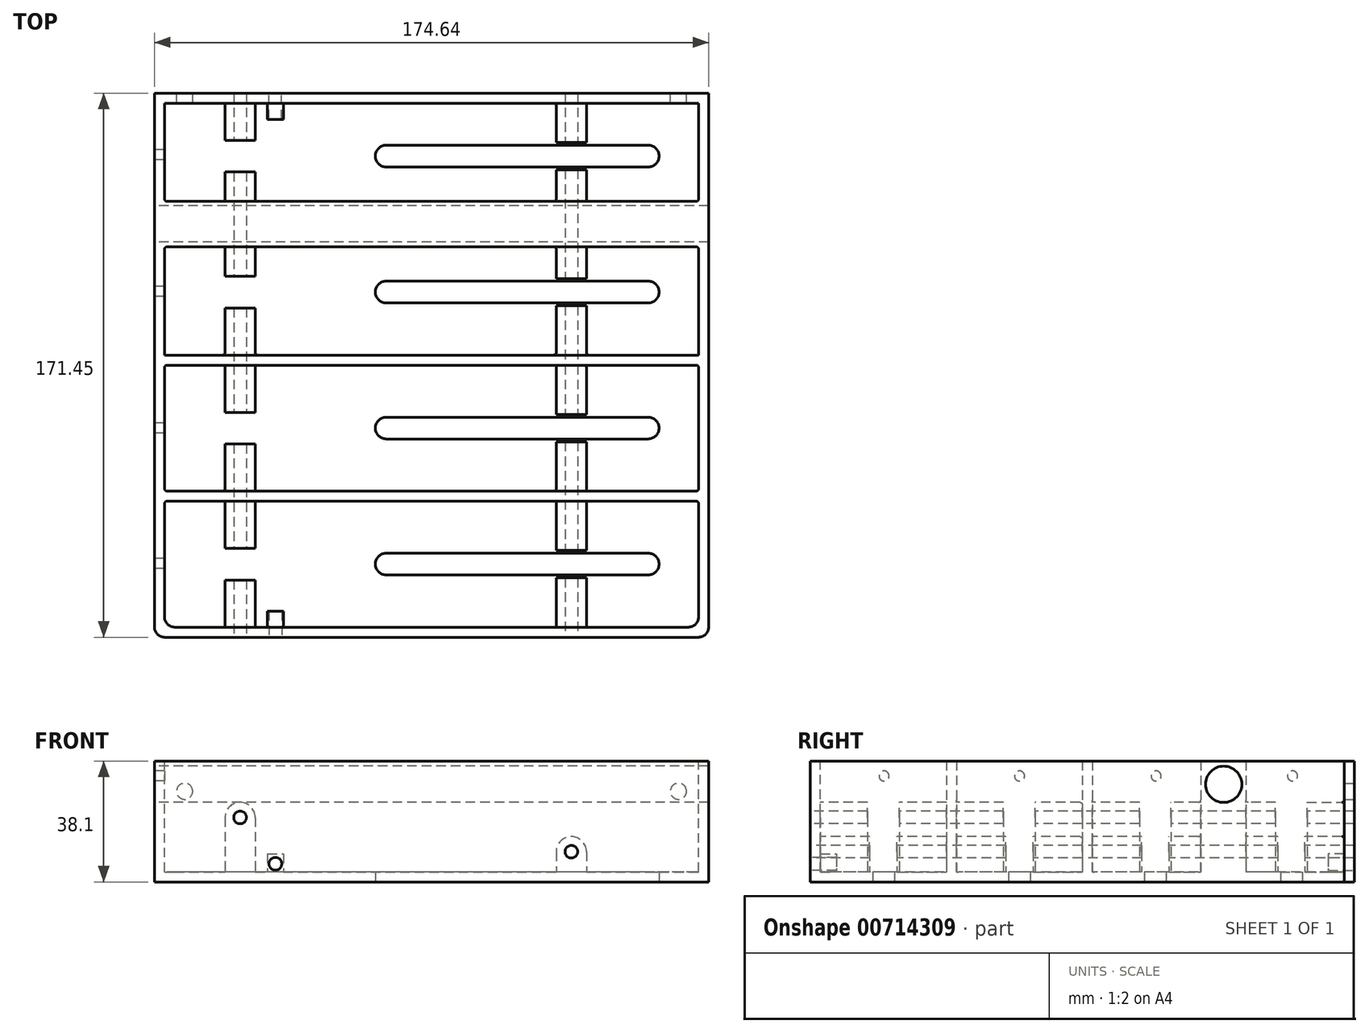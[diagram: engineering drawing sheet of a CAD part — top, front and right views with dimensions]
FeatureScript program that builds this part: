
annotation { "Feature Type Name" : "Feature", "Feature Type Description" : "" }
export const myFeature = defineFeature(function(context is Context, id is Id, definition is map)
    precondition{}
    {
        {
            var Q0;
            Q0=qCreatedBy(makeId("Top.planeOp"),FACE);
            var sketch = newSketch(context, id + "F0", { "sketchPlane" : qUnion([Q0])});
            skLineSegment(sketch, "E0.bottom", {"start": v(0, 0) * mm, "end": v(174.63, 0) * mm});
            skLineSegment(sketch, "E0.top", {"start": v(0, 174.63) * mm, "end": v(174.62, 174.63) * mm});
            skLineSegment(sketch, "E0.left", {"start": v(0, 0) * mm, "end": v(0, 174.63) * mm});
            skLineSegment(sketch, "E0.right", {"start": v(174.63, 0) * mm, "end": v(174.62, 174.63) * mm});
            skSolve(sketch);
        }
        {
            var Q0;
            Q0 = qSketchRegion(id + "F0", true);
            extrude(context, id + "F1", {"entities" : qUnion([Q0]), "depth" : 38.1 * mm, "offsetDistance" : 25.4 * mm});
        }
        {
            var Q0;
            Q0=makeQuery(id+"F1.opExtrude","CAP_FACE",FACE,{"disambiguationData":[OSD([sQuery(id+"F0.wireOp",EDGE,"E0.bottom"),sQuery(id+"F0.wireOp",EDGE,"E0.top"),sQuery(id+"F0.wireOp",EDGE,"E0.left"),sQuery(id+"F0.wireOp",EDGE,"E0.right")])],"isStart":false});
            var sketch = newSketch(context, id + "F2", { "sketchPlane" : qUnion([Q0])});
            skLineSegment(sketch, "E1.bottom", {"start": v(3.17, 171.45) * mm, "end": v(171.45, 171.45) * mm});
            skLineSegment(sketch, "E1.top", {"start": v(3.18, 3.18) * mm, "end": v(171.45, 3.18) * mm});
            skLineSegment(sketch, "E1.left", {"start": v(3.17, 171.45) * mm, "end": v(3.18, 3.17) * mm});
            skLineSegment(sketch, "E1.right", {"start": v(171.45, 171.45) * mm, "end": v(171.45, 3.18) * mm});
            skSolve(sketch);
        }
        {
            var Q0;
            Q0 = qSketchRegion(id + "F2", true);
            extrude(context, id + "F3", {"entities" : qUnion([Q0]), "operationType" : NewBodyOperationType.REMOVE, "oppositeDirection" : true, "depth" : 34.92 * mm, "offsetDistance" : 25.4 * mm});
        }
        {
            var Q0;
            Q0=makeQuery(id+"F3.boolean.opBoolean","COPY",EDGE,{"derivedFrom":makeQuery(id+"F3.opExtrude","SWEPT_EDGE",EDGE,{"disambiguationData":[OSD([sQuery(id+"F2.wireOp",EDGE,"E1.bottom"),sQuery(id+"F2.wireOp",EDGE,"E1.right")])]})});
            var Q1;
            Q1=makeQuery(id+"F3.boolean.opBoolean","COPY",EDGE,{"derivedFrom":makeQuery(id+"F3.opExtrude","SWEPT_EDGE",EDGE,{"disambiguationData":[OSD([sQuery(id+"F2.wireOp",EDGE,"E1.top"),sQuery(id+"F2.wireOp",EDGE,"E1.right")])]})});
            var Q2;
            Q2=makeQuery(id+"F3.boolean.opBoolean","COPY",EDGE,{"derivedFrom":makeQuery(id+"F3.opExtrude","SWEPT_EDGE",EDGE,{"disambiguationData":[OSD([sQuery(id+"F2.wireOp",EDGE,"E1.bottom"),sQuery(id+"F2.wireOp",EDGE,"E1.left")])]})});
            var Q3;
            Q3=makeQuery(id+"F3.boolean.opBoolean","COPY",EDGE,{"derivedFrom":makeQuery(id+"F3.opExtrude","SWEPT_EDGE",EDGE,{"disambiguationData":[OSD([sQuery(id+"F2.wireOp",EDGE,"E1.top"),sQuery(id+"F2.wireOp",EDGE,"E1.left")])]})});
            var Q4;
            Q4=makeQuery(id+"F1.opExtrude","SWEPT_EDGE",EDGE,{"disambiguationData":[OSD([sQuery(id+"F0.wireOp",EDGE,"E0.top"),sQuery(id+"F0.wireOp",EDGE,"E0.right")])]});
            var Q5;
            Q5=makeQuery(id+"F1.opExtrude","SWEPT_EDGE",EDGE,{"disambiguationData":[OSD([sQuery(id+"F0.wireOp",EDGE,"E0.top"),sQuery(id+"F0.wireOp",EDGE,"E0.left")])]});
            var Q6;
            Q6=makeQuery(id+"F1.opExtrude","SWEPT_EDGE",EDGE,{"disambiguationData":[OSD([sQuery(id+"F0.wireOp",EDGE,"E0.bottom"),sQuery(id+"F0.wireOp",EDGE,"E0.right")])]});
            var Q7;
            Q7=makeQuery(id+"F1.opExtrude","SWEPT_EDGE",EDGE,{"disambiguationData":[OSD([sQuery(id+"F0.wireOp",EDGE,"E0.bottom"),sQuery(id+"F0.wireOp",EDGE,"E0.left")])]});
            fillet(context, id + "F4", {"entities" : qUnion([Q0, Q1, Q2, Q3, Q4, Q5, Q6, Q7]), "radius" : 3.17 * mm, "tangentPropagation" : true, "allowEdgeOverflow" : false});
        }
        {
            var Q0;
            Q0=qCreatedBy(makeId("Top.planeOp"),FACE);
            var sketch = newSketch(context, id + "F5", { "sketchPlane" : qUnion([Q0])});
            skLineSegment(sketch, "E2.bottom", {"start": v(3.36, 131.76) * mm, "end": v(171.33, 131.76) * mm});
            skLineSegment(sketch, "E2.top", {"start": v(3.36, 128.59) * mm, "end": v(171.33, 128.59) * mm});
            skLineSegment(sketch, "E2.left", {"start": v(3.36, 131.76) * mm, "end": v(3.36, 128.59) * mm});
            skLineSegment(sketch, "E2.right", {"start": v(171.33, 131.76) * mm, "end": v(171.33, 128.59) * mm});
            skLineSegment(sketch, "E3.bottom", {"start": v(3.17, 88.9) * mm, "end": v(171.45, 88.9) * mm});
            skLineSegment(sketch, "E3.top", {"start": v(3.17, 85.72) * mm, "end": v(171.45, 85.72) * mm});
            skLineSegment(sketch, "E3.left", {"start": v(3.17, 88.9) * mm, "end": v(3.17, 85.72) * mm});
            skLineSegment(sketch, "E3.right", {"start": v(171.45, 88.9) * mm, "end": v(171.45, 85.73) * mm});
            skLineSegment(sketch, "E4.bottom", {"start": v(3.18, 46.04) * mm, "end": v(171.45, 46.04) * mm});
            skLineSegment(sketch, "E4.top", {"start": v(3.18, 42.86) * mm, "end": v(171.45, 42.86) * mm});
            skLineSegment(sketch, "E4.left", {"start": v(3.18, 46.04) * mm, "end": v(3.18, 42.86) * mm});
            skLineSegment(sketch, "E4.right", {"start": v(171.45, 46.04) * mm, "end": v(171.45, 42.86) * mm});
            skSolve(sketch);
        }
        {
            var Q0;
            Q0 = qSketchRegion(id + "F5", true);
            extrude(context, id + "F6", {"entities" : qUnion([Q0]), "operationType" : NewBodyOperationType.ADD, "depth" : 38.1 * mm, "offsetDistance" : 25.4 * mm});
        }
        {
            var Q0;
            Q0=qCreatedBy(makeId("Top.planeOp"),FACE);
            var sketch = newSketch(context, id + "F7", { "sketchPlane" : qUnion([Q0])});
            skLineSegment(sketch, "E5", {"start": v(73.02, 155.03) * mm, "end": v(155.57, 155.03) * mm});
            skArc(sketch, "E6", {"start": v(155.57, 148.17) * mm, "mid": v(159, 151.6) * mm, "end": v(155.57, 155.03) * mm});
            skLineSegment(sketch, "E7", {"start": v(155.57, 148.17) * mm, "end": v(73.02, 148.17) * mm});
            skArc(sketch, "E8", {"start": v(73.02, 155.03) * mm, "mid": v(69.6, 151.6) * mm, "end": v(73.02, 148.17) * mm});
            skLineSegment(sketch, "E9.0.1.0", {"start": v(155.57, 105.32) * mm, "end": v(73.02, 105.32) * mm});
            skArc(sketch, "E9.0.1.1", {"start": v(155.57, 105.32) * mm, "mid": v(159, 108.75) * mm, "end": v(155.57, 112.18) * mm});
            skLineSegment(sketch, "E9.0.1.2", {"start": v(73.02, 112.18) * mm, "end": v(155.57, 112.18) * mm});
            skArc(sketch, "E9.0.1.3", {"start": v(73.02, 112.18) * mm, "mid": v(69.6, 108.75) * mm, "end": v(73.02, 105.32) * mm});
            skLineSegment(sketch, "E9.0.2.0", {"start": v(155.57, 62.47) * mm, "end": v(73.02, 62.47) * mm});
            skArc(sketch, "E9.0.2.1", {"start": v(155.57, 62.47) * mm, "mid": v(159, 65.9) * mm, "end": v(155.57, 69.33) * mm});
            skLineSegment(sketch, "E9.0.2.2", {"start": v(73.02, 69.33) * mm, "end": v(155.57, 69.33) * mm});
            skArc(sketch, "E9.0.2.3", {"start": v(73.02, 69.33) * mm, "mid": v(69.6, 65.9) * mm, "end": v(73.02, 62.47) * mm});
            skLineSegment(sketch, "E9.0.3.0", {"start": v(155.57, 19.62) * mm, "end": v(73.02, 19.62) * mm});
            skArc(sketch, "E9.0.3.1", {"start": v(155.57, 19.62) * mm, "mid": v(159, 23.05) * mm, "end": v(155.57, 26.48) * mm});
            skLineSegment(sketch, "E9.0.3.2", {"start": v(73.02, 26.48) * mm, "end": v(155.57, 26.48) * mm});
            skArc(sketch, "E9.0.3.3", {"start": v(73.02, 26.48) * mm, "mid": v(69.6, 23.05) * mm, "end": v(73.02, 19.62) * mm});
            skLineSegment(sketch, "E9.direction1", {"start": v(73.02, 148.17) * mm, "end": v(73.02, 148.17) * mm});
            skLineSegment(sketch, "E9.direction2", {"start": v(73.02, 148.17) * mm, "end": v(73.02, 105.32) * mm, "construction": true});
            skSolve(sketch);
        }
        {
            var Q0;
            Q0 = qSketchRegion(id + "F7", true);
            extrude(context, id + "F8", {"entities" : qUnion([Q0]), "operationType" : NewBodyOperationType.REMOVE, "depth" : 5.08 * mm, "offsetDistance" : 25.4 * mm});
        }
        {
            var Q0;
            Q0=makeQuery(id+"F1.opExtrude","SWEPT_FACE",FACE,{"disambiguationData":[OSD([sQuery(id+"F0.wireOp",EDGE,"E0.bottom")])]});
            var sketch = newSketch(context, id + "F9", { "sketchPlane" : qUnion([Q0])});
            skCircle(sketch, "E10", {"center": v(131.36, 9.53) * mm, "radius": 2 * mm});
            skCircle(sketch, "E11", {"center": v(26.99, 20.32) * mm, "radius": 2 * mm});
            skSolve(sketch);
        }
        {
            var Q0;
            Q0=qCreatedBy(makeId("Top.planeOp"),FACE);
            var sketch = newSketch(context, id + "F10", { "sketchPlane" : qUnion([Q0])});
            skLineSegment(sketch, "E12.bottom", {"start": v(22.23, 3.18) * mm, "end": v(31.75, 3.18) * mm});
            skLineSegment(sketch, "E12.top", {"start": v(22.23, 18.03) * mm, "end": v(31.75, 18.03) * mm});
            skLineSegment(sketch, "E12.left", {"start": v(22.23, 3.18) * mm, "end": v(22.23, 18.03) * mm});
            skLineSegment(sketch, "E12.right", {"start": v(31.75, 3.18) * mm, "end": v(31.75, 18.03) * mm});
            skLineSegment(sketch, "E13.bottom", {"start": v(22.23, 42.86) * mm, "end": v(31.75, 42.86) * mm});
            skLineSegment(sketch, "E13.top", {"start": v(22.23, 28) * mm, "end": v(31.75, 28) * mm});
            skLineSegment(sketch, "E13.left", {"start": v(22.23, 42.86) * mm, "end": v(22.23, 28) * mm});
            skLineSegment(sketch, "E13.right", {"start": v(31.75, 42.86) * mm, "end": v(31.75, 28) * mm});
            skLineSegment(sketch, "E14.0.1.0", {"start": v(31.75, 46.02) * mm, "end": v(31.75, 60.88) * mm});
            skLineSegment(sketch, "E14.0.1.1", {"start": v(22.23, 60.88) * mm, "end": v(31.75, 60.88) * mm});
            skLineSegment(sketch, "E14.0.1.2", {"start": v(22.23, 46.02) * mm, "end": v(22.23, 60.88) * mm});
            skLineSegment(sketch, "E14.0.1.3", {"start": v(22.23, 46.02) * mm, "end": v(31.75, 46.02) * mm});
            skLineSegment(sketch, "E14.0.1.4", {"start": v(22.23, 70.85) * mm, "end": v(31.75, 70.85) * mm});
            skLineSegment(sketch, "E14.0.1.5", {"start": v(31.75, 85.71) * mm, "end": v(31.75, 70.85) * mm});
            skLineSegment(sketch, "E14.0.1.6", {"start": v(22.23, 85.71) * mm, "end": v(22.23, 70.85) * mm});
            skLineSegment(sketch, "E14.0.1.7", {"start": v(22.23, 85.71) * mm, "end": v(31.75, 85.71) * mm});
            skLineSegment(sketch, "E14.0.2.0", {"start": v(31.75, 88.87) * mm, "end": v(31.75, 103.73) * mm});
            skLineSegment(sketch, "E14.0.2.1", {"start": v(22.23, 103.73) * mm, "end": v(31.75, 103.73) * mm});
            skLineSegment(sketch, "E14.0.2.2", {"start": v(22.23, 88.87) * mm, "end": v(22.23, 103.73) * mm});
            skLineSegment(sketch, "E14.0.2.3", {"start": v(22.23, 88.87) * mm, "end": v(31.75, 88.87) * mm});
            skLineSegment(sketch, "E14.0.2.4", {"start": v(22.23, 113.7) * mm, "end": v(31.75, 113.7) * mm});
            skLineSegment(sketch, "E14.0.2.5", {"start": v(31.75, 128.56) * mm, "end": v(31.75, 113.7) * mm});
            skLineSegment(sketch, "E14.0.2.6", {"start": v(22.23, 128.56) * mm, "end": v(22.23, 113.7) * mm});
            skLineSegment(sketch, "E14.0.2.7", {"start": v(22.23, 128.56) * mm, "end": v(31.75, 128.56) * mm});
            skLineSegment(sketch, "E14.0.3.0", {"start": v(31.75, 131.72) * mm, "end": v(31.75, 146.58) * mm});
            skLineSegment(sketch, "E14.0.3.1", {"start": v(22.23, 146.58) * mm, "end": v(31.75, 146.58) * mm});
            skLineSegment(sketch, "E14.0.3.2", {"start": v(22.23, 131.72) * mm, "end": v(22.23, 146.58) * mm});
            skLineSegment(sketch, "E14.0.3.3", {"start": v(22.23, 131.72) * mm, "end": v(31.75, 131.72) * mm});
            skLineSegment(sketch, "E14.0.3.4", {"start": v(22.23, 156.55) * mm, "end": v(31.75, 156.55) * mm});
            skLineSegment(sketch, "E14.0.3.5", {"start": v(31.75, 171.41) * mm, "end": v(31.75, 156.55) * mm});
            skLineSegment(sketch, "E14.0.3.6", {"start": v(22.23, 171.41) * mm, "end": v(22.23, 156.55) * mm});
            skLineSegment(sketch, "E14.0.3.7", {"start": v(22.23, 171.41) * mm, "end": v(31.75, 171.41) * mm});
            skLineSegment(sketch, "E14.direction1", {"start": v(31.75, 3.18) * mm, "end": v(31.75, 3.18) * mm});
            skSolve(sketch);
        }
        {
            var Q0;
            Q0 = qSketchRegion(id + "F10", true);
            extrude(context, id + "F11", {"entities" : qUnion([Q0]), "operationType" : NewBodyOperationType.ADD, "depth" : 25.1 * mm, "offsetDistance" : 25.4 * mm});
        }
        {
            var Q0;
            Q0=makeQuery(id+"F11.opExtrude","CAP_EDGE",EDGE,{"disambiguationData":[OSD([sQuery(id+"F10.wireOp",EDGE,"E14.0.3.6")])],"isStart":false});
            var Q1;
            Q1=makeQuery(id+"F11.opExtrude","CAP_EDGE",EDGE,{"disambiguationData":[OSD([sQuery(id+"F10.wireOp",EDGE,"E14.0.3.5")])],"isStart":false});
            var Q2;
            Q2=makeQuery(id+"F11.opExtrude","CAP_EDGE",EDGE,{"disambiguationData":[OSD([sQuery(id+"F10.wireOp",EDGE,"E14.0.3.0")])],"isStart":false});
            var Q3;
            Q3=makeQuery(id+"F11.opExtrude","CAP_EDGE",EDGE,{"disambiguationData":[OSD([sQuery(id+"F10.wireOp",EDGE,"E14.0.3.2")])],"isStart":false});
            var Q4;
            Q4=makeQuery(id+"F11.opExtrude","CAP_EDGE",EDGE,{"disambiguationData":[OSD([sQuery(id+"F10.wireOp",EDGE,"E14.0.2.5")])],"isStart":false});
            var Q5;
            Q5=makeQuery(id+"F11.opExtrude","CAP_EDGE",EDGE,{"disambiguationData":[OSD([sQuery(id+"F10.wireOp",EDGE,"E14.0.2.0")])],"isStart":false});
            var Q6;
            Q6=makeQuery(id+"F11.opExtrude","CAP_EDGE",EDGE,{"disambiguationData":[OSD([sQuery(id+"F10.wireOp",EDGE,"E14.0.1.5")])],"isStart":false});
            var Q7;
            Q7=makeQuery(id+"F11.opExtrude","CAP_EDGE",EDGE,{"disambiguationData":[OSD([sQuery(id+"F10.wireOp",EDGE,"E14.0.1.0")])],"isStart":false});
            var Q8;
            Q8=makeQuery(id+"F11.opExtrude","CAP_EDGE",EDGE,{"disambiguationData":[OSD([sQuery(id+"F10.wireOp",EDGE,"E13.right")])],"isStart":false});
            var Q9;
            Q9=makeQuery(id+"F11.opExtrude","CAP_EDGE",EDGE,{"disambiguationData":[OSD([sQuery(id+"F10.wireOp",EDGE,"E12.right")])],"isStart":false});
            var Q10;
            Q10=makeQuery(id+"F11.opExtrude","CAP_EDGE",EDGE,{"disambiguationData":[OSD([sQuery(id+"F10.wireOp",EDGE,"E14.0.2.6")])],"isStart":false});
            var Q11;
            Q11=makeQuery(id+"F11.opExtrude","CAP_EDGE",EDGE,{"disambiguationData":[OSD([sQuery(id+"F10.wireOp",EDGE,"E14.0.1.6")])],"isStart":false});
            var Q12;
            Q12=makeQuery(id+"F11.opExtrude","CAP_EDGE",EDGE,{"disambiguationData":[OSD([sQuery(id+"F10.wireOp",EDGE,"E14.0.2.2")])],"isStart":false});
            var Q13;
            Q13=makeQuery(id+"F11.opExtrude","CAP_EDGE",EDGE,{"disambiguationData":[OSD([sQuery(id+"F10.wireOp",EDGE,"E14.0.1.2")])],"isStart":false});
            var Q14;
            Q14=makeQuery(id+"F11.opExtrude","CAP_EDGE",EDGE,{"disambiguationData":[OSD([sQuery(id+"F10.wireOp",EDGE,"E13.left")])],"isStart":false});
            var Q15;
            Q15=makeQuery(id+"F11.opExtrude","CAP_EDGE",EDGE,{"disambiguationData":[OSD([sQuery(id+"F10.wireOp",EDGE,"E12.left")])],"isStart":false});
            fillet(context, id + "F12", {"entities" : qUnion([Q0, Q1, Q2, Q3, Q4, Q5, Q6, Q7, Q8, Q9, Q10, Q11, Q12, Q13, Q14, Q15]), "radius" : 4.76 * mm, "tangentPropagation" : true, "allowEdgeOverflow" : false});
        }
        {
            var Q0;
            Q0=makeQuery(id+"F1.opExtrude","CAP_FACE",FACE,{"disambiguationData":[OSD([sQuery(id+"F0.wireOp",EDGE,"E0.bottom"),sQuery(id+"F0.wireOp",EDGE,"E0.top"),sQuery(id+"F0.wireOp",EDGE,"E0.left"),sQuery(id+"F0.wireOp",EDGE,"E0.right")])],"isStart":true});
            var sketch = newSketch(context, id + "F13", { "sketchPlane" : qUnion([Q0])});
            skLineSegment(sketch, "E15.bottom", {"start": v(126.6, -3.18) * mm, "end": v(136.12, -3.18) * mm});
            skLineSegment(sketch, "E15.top", {"start": v(126.6, -18.72) * mm, "end": v(136.12, -18.72) * mm});
            skLineSegment(sketch, "E15.left", {"start": v(126.6, -3.18) * mm, "end": v(126.6, -18.72) * mm});
            skLineSegment(sketch, "E15.right", {"start": v(136.12, -3.18) * mm, "end": v(136.12, -18.72) * mm});
            skLineSegment(sketch, "E16.bottom", {"start": v(126.6, -42.86) * mm, "end": v(136.12, -42.86) * mm});
            skLineSegment(sketch, "E16.top", {"start": v(126.6, -27.32) * mm, "end": v(136.12, -27.32) * mm});
            skLineSegment(sketch, "E16.left", {"start": v(126.6, -42.86) * mm, "end": v(126.6, -27.32) * mm});
            skLineSegment(sketch, "E16.right", {"start": v(136.12, -42.86) * mm, "end": v(136.12, -27.32) * mm});
            skLineSegment(sketch, "E17.0.1.0", {"start": v(136.12, -46.02) * mm, "end": v(136.12, -61.57) * mm});
            skLineSegment(sketch, "E17.0.1.1", {"start": v(126.6, -46.02) * mm, "end": v(136.12, -46.02) * mm});
            skLineSegment(sketch, "E17.0.1.2", {"start": v(126.6, -46.02) * mm, "end": v(126.6, -61.57) * mm});
            skLineSegment(sketch, "E17.0.1.3", {"start": v(126.6, -61.57) * mm, "end": v(136.12, -61.57) * mm});
            skLineSegment(sketch, "E17.0.1.4", {"start": v(136.12, -85.71) * mm, "end": v(136.12, -70.17) * mm});
            skLineSegment(sketch, "E17.0.1.5", {"start": v(126.6, -85.71) * mm, "end": v(126.6, -70.17) * mm});
            skLineSegment(sketch, "E17.0.1.6", {"start": v(126.6, -70.17) * mm, "end": v(136.12, -70.17) * mm});
            skLineSegment(sketch, "E17.0.1.7", {"start": v(126.6, -85.71) * mm, "end": v(136.12, -85.71) * mm});
            skLineSegment(sketch, "E17.0.2.0", {"start": v(136.12, -88.87) * mm, "end": v(136.12, -104.42) * mm});
            skLineSegment(sketch, "E17.0.2.1", {"start": v(126.6, -88.87) * mm, "end": v(136.12, -88.87) * mm});
            skLineSegment(sketch, "E17.0.2.2", {"start": v(126.6, -88.87) * mm, "end": v(126.6, -104.42) * mm});
            skLineSegment(sketch, "E17.0.2.3", {"start": v(126.6, -104.42) * mm, "end": v(136.12, -104.42) * mm});
            skLineSegment(sketch, "E17.0.2.4", {"start": v(136.12, -128.56) * mm, "end": v(136.12, -113.02) * mm});
            skLineSegment(sketch, "E17.0.2.5", {"start": v(126.6, -128.56) * mm, "end": v(126.6, -113.02) * mm});
            skLineSegment(sketch, "E17.0.2.6", {"start": v(126.6, -113.02) * mm, "end": v(136.12, -113.02) * mm});
            skLineSegment(sketch, "E17.0.2.7", {"start": v(126.6, -128.56) * mm, "end": v(136.12, -128.56) * mm});
            skLineSegment(sketch, "E17.0.3.0", {"start": v(136.12, -131.72) * mm, "end": v(136.12, -147.27) * mm});
            skLineSegment(sketch, "E17.0.3.1", {"start": v(126.6, -131.72) * mm, "end": v(136.12, -131.72) * mm});
            skLineSegment(sketch, "E17.0.3.2", {"start": v(126.6, -131.72) * mm, "end": v(126.6, -147.27) * mm});
            skLineSegment(sketch, "E17.0.3.3", {"start": v(126.6, -147.27) * mm, "end": v(136.12, -147.27) * mm});
            skLineSegment(sketch, "E17.0.3.4", {"start": v(136.12, -171.41) * mm, "end": v(136.12, -155.87) * mm});
            skLineSegment(sketch, "E17.0.3.5", {"start": v(126.6, -171.41) * mm, "end": v(126.6, -155.87) * mm});
            skLineSegment(sketch, "E17.0.3.6", {"start": v(126.6, -155.87) * mm, "end": v(136.12, -155.87) * mm});
            skLineSegment(sketch, "E17.0.3.7", {"start": v(126.6, -171.41) * mm, "end": v(136.12, -171.41) * mm});
            skLineSegment(sketch, "E17.direction1", {"start": v(136.12, -18.72) * mm, "end": v(161.52, -18.72) * mm, "construction": true});
            skLineSegment(sketch, "E17.direction2", {"start": v(136.12, -18.72) * mm, "end": v(136.12, -61.57) * mm, "construction": true});
            skSolve(sketch);
        }
        {
            var Q0;
            Q0 = qSketchRegion(id + "F13", true);
            extrude(context, id + "F14", {"entities" : qUnion([Q0]), "operationType" : NewBodyOperationType.ADD, "oppositeDirection" : true, "depth" : 14.29 * mm, "offsetDistance" : 25.4 * mm});
        }
        {
            var Q0;
            Q0=makeQuery(id+"F14.opExtrude","CAP_EDGE",EDGE,{"disambiguationData":[OSD([sQuery(id+"F13.wireOp",EDGE,"E17.0.3.5")])],"isStart":false});
            var Q1;
            Q1=makeQuery(id+"F14.opExtrude","CAP_EDGE",EDGE,{"disambiguationData":[OSD([sQuery(id+"F13.wireOp",EDGE,"E17.0.3.2")])],"isStart":false});
            var Q2;
            Q2=makeQuery(id+"F14.opExtrude","CAP_EDGE",EDGE,{"disambiguationData":[OSD([sQuery(id+"F13.wireOp",EDGE,"E17.0.2.5")])],"isStart":false});
            var Q3;
            Q3=makeQuery(id+"F14.opExtrude","CAP_EDGE",EDGE,{"disambiguationData":[OSD([sQuery(id+"F13.wireOp",EDGE,"E17.0.2.2")])],"isStart":false});
            var Q4;
            Q4=makeQuery(id+"F14.opExtrude","CAP_EDGE",EDGE,{"disambiguationData":[OSD([sQuery(id+"F13.wireOp",EDGE,"E17.0.1.5")])],"isStart":false});
            var Q5;
            Q5=makeQuery(id+"F14.opExtrude","CAP_EDGE",EDGE,{"disambiguationData":[OSD([sQuery(id+"F13.wireOp",EDGE,"E17.0.1.2")])],"isStart":false});
            var Q6;
            Q6=makeQuery(id+"F14.opExtrude","CAP_EDGE",EDGE,{"disambiguationData":[OSD([sQuery(id+"F13.wireOp",EDGE,"E16.left")])],"isStart":false});
            var Q7;
            Q7=makeQuery(id+"F14.opExtrude","CAP_EDGE",EDGE,{"disambiguationData":[OSD([sQuery(id+"F13.wireOp",EDGE,"E15.left")])],"isStart":false});
            var Q8;
            Q8=makeQuery(id+"F14.opExtrude","CAP_EDGE",EDGE,{"disambiguationData":[OSD([sQuery(id+"F13.wireOp",EDGE,"E15.right")])],"isStart":false});
            var Q9;
            Q9=makeQuery(id+"F14.opExtrude","CAP_EDGE",EDGE,{"disambiguationData":[OSD([sQuery(id+"F13.wireOp",EDGE,"E16.right")])],"isStart":false});
            var Q10;
            Q10=makeQuery(id+"F14.opExtrude","CAP_EDGE",EDGE,{"disambiguationData":[OSD([sQuery(id+"F13.wireOp",EDGE,"E17.0.1.0")])],"isStart":false});
            var Q11;
            Q11=makeQuery(id+"F14.opExtrude","CAP_EDGE",EDGE,{"disambiguationData":[OSD([sQuery(id+"F13.wireOp",EDGE,"E17.0.1.4")])],"isStart":false});
            var Q12;
            Q12=makeQuery(id+"F14.opExtrude","CAP_EDGE",EDGE,{"disambiguationData":[OSD([sQuery(id+"F13.wireOp",EDGE,"E17.0.2.0")])],"isStart":false});
            var Q13;
            Q13=makeQuery(id+"F14.opExtrude","CAP_EDGE",EDGE,{"disambiguationData":[OSD([sQuery(id+"F13.wireOp",EDGE,"E17.0.2.4")])],"isStart":false});
            var Q14;
            Q14=makeQuery(id+"F14.opExtrude","CAP_EDGE",EDGE,{"disambiguationData":[OSD([sQuery(id+"F13.wireOp",EDGE,"E17.0.3.0")])],"isStart":false});
            var Q15;
            Q15=makeQuery(id+"F14.opExtrude","CAP_EDGE",EDGE,{"disambiguationData":[OSD([sQuery(id+"F13.wireOp",EDGE,"E17.0.3.4")])],"isStart":false});
            fillet(context, id + "F15", {"entities" : qUnion([Q0, Q1, Q2, Q3, Q4, Q5, Q6, Q7, Q8, Q9, Q10, Q11, Q12, Q13, Q14, Q15]), "radius" : 4.76 * mm, "tangentPropagation" : true, "allowEdgeOverflow" : false});
        }
        {
            var Q0;
            Q0=makeQuery(id+"F1.opExtrude","SWEPT_FACE",FACE,{"disambiguationData":[OSD([sQuery(id+"F0.wireOp",EDGE,"E0.bottom")])]});
            var sketch = newSketch(context, id + "F16", { "sketchPlane" : qUnion([Q0])});
            skCircle(sketch, "E18", {"center": v(38.1, 5.72) * mm, "radius": 2.02 * mm});
            skSolve(sketch);
        }
        {
            var Q0;
            Q0=qCreatedBy(makeId("Top.planeOp"),FACE);
            var sketch = newSketch(context, id + "F17", { "sketchPlane" : qUnion([Q0])});
            skLineSegment(sketch, "E19.bottom", {"start": v(0, 171.45) * mm, "end": v(174.64, 171.45) * mm});
            skLineSegment(sketch, "E19.top", {"start": v(0, 168.28) * mm, "end": v(174.64, 168.28) * mm});
            skLineSegment(sketch, "E19.left", {"start": v(0, 171.45) * mm, "end": v(0, 168.28) * mm});
            skLineSegment(sketch, "E19.right", {"start": v(174.64, 171.45) * mm, "end": v(174.64, 168.28) * mm});
            skSolve(sketch);
        }
        {
            var Q0;
            Q0 = qSketchRegion(id + "F17", true);
            extrude(context, id + "F18", {"entities" : qUnion([Q0]), "operationType" : NewBodyOperationType.ADD, "depth" : 38.1 * mm, "offsetDistance" : 25.4 * mm});
        }
        {
            var Q0;
            Q0=qCreatedBy(makeId("Top.planeOp"),FACE);
            var sketch = newSketch(context, id + "F19", { "sketchPlane" : qUnion([Q0])});
            skLineSegment(sketch, "E20", {"start": v(0, 171.45) * mm, "end": v(177.9, 171.45) * mm});
            skLineSegment(sketch, "E21", {"start": v(174.94, 171.45) * mm, "end": v(174.94, 175.26) * mm});
            skLineSegment(sketch, "E22", {"start": v(174.94, 175.26) * mm, "end": v(0, 175.26) * mm});
            skLineSegment(sketch, "E23", {"start": v(0, 175.26) * mm, "end": v(0, 171.45) * mm});
            skSolve(sketch);
        }
        {
            var Q0;
            {var subQ2=sQuery(id+"F19.wireOp",EDGE,"E21");Q0=makeQuery(id+"F19.imprint","IMPRINT",FACE,{"disambiguationData":[TD([[makeQuery(id+"F19.imprint","IMPRINT",EDGE,{"derivedFrom":subQ2}),1.0]])]});}
            extrude(context, id + "F20", {"entities" : qUnion([Q0]), "operationType" : NewBodyOperationType.REMOVE, "depth" : 38.1 * mm, "offsetDistance" : 25.4 * mm});
        }
        {
            var Q0;
            Q0=qCreatedBy(makeId("Top.planeOp"),FACE);
            var sketch = newSketch(context, id + "F21", { "sketchPlane" : qUnion([Q0])});
            skLineSegment(sketch, "E24.bottom", {"start": v(2.63, 137.31) * mm, "end": v(173.93, 137.31) * mm});
            skLineSegment(sketch, "E24.top", {"start": v(2.63, 123.02) * mm, "end": v(173.93, 123.02) * mm});
            skLineSegment(sketch, "E24.left", {"start": v(2.63, 137.31) * mm, "end": v(2.63, 123.02) * mm});
            skLineSegment(sketch, "E24.right", {"start": v(173.93, 137.31) * mm, "end": v(173.93, 123.02) * mm});
            skSolve(sketch);
        }
        {
            var Q0;
            Q0 = qSketchRegion(id + "F21", true);
            extrude(context, id + "F22", {"entities" : qUnion([Q0]), "operationType" : NewBodyOperationType.ADD, "depth" : 38.1 * mm, "offsetDistance" : 25.4 * mm});
        }
        {
            var Q0;
            Q0=makeQuery(id+"F18.boolean.opBoolean","INTERSECT",EDGE,{"derivedFrom":[makeQuery(id+"F11.opExtrude","SWEPT_FACE",FACE,{"disambiguationData":[OSD([sQuery(id+"F10.wireOp",EDGE,"E14.0.3.5")])]}),makeQuery(id+"F18.opExtrude","SWEPT_FACE",FACE,{"disambiguationData":[OSD([sQuery(id+"F17.wireOp",EDGE,"E19.top")])]})]});
            var Q1;
            Q1=makeQuery(id+"F18.boolean.opBoolean","INTERSECT",EDGE,{"derivedFrom":[makeQuery(id+"F14.opExtrude","SWEPT_FACE",FACE,{"disambiguationData":[OSD([sQuery(id+"F13.wireOp",EDGE,"E17.0.3.4")])]}),makeQuery(id+"F18.opExtrude","SWEPT_FACE",FACE,{"disambiguationData":[OSD([sQuery(id+"F17.wireOp",EDGE,"E19.top")])]})]});
            var Q2;
            Q2=makeQuery(id+"F18.boolean.opBoolean","INTERSECT",EDGE,{"derivedFrom":[makeQuery(id+"F15.opFillet","BLEND_FACE",FACE,{"disambiguationData":[OSD([sQuery(id+"F13.wireOp",EDGE,"E17.0.3.5")])]}),makeQuery(id+"F18.opExtrude","SWEPT_FACE",FACE,{"disambiguationData":[OSD([sQuery(id+"F17.wireOp",EDGE,"E19.top")])]})]});
            var Q3;
            Q3=makeQuery(id+"F18.boolean.opBoolean","INTERSECT",EDGE,{"derivedFrom":[makeQuery(id+"F14.opExtrude","SWEPT_FACE",FACE,{"disambiguationData":[OSD([sQuery(id+"F13.wireOp",EDGE,"E17.0.3.5")])]}),makeQuery(id+"F18.opExtrude","SWEPT_FACE",FACE,{"disambiguationData":[OSD([sQuery(id+"F17.wireOp",EDGE,"E19.top")])]})]});
            var Q4;
            Q4=makeQuery(id+"F22.boolean.opBoolean","INTERSECT",EDGE,{"derivedFrom":[makeQuery(id+"F11.opExtrude","SWEPT_FACE",FACE,{"disambiguationData":[OSD([sQuery(id+"F10.wireOp",EDGE,"E14.0.3.0")])]}),makeQuery(id+"F22.opExtrude","SWEPT_FACE",FACE,{"disambiguationData":[OSD([sQuery(id+"F21.wireOp",EDGE,"E24.bottom")])]})]});
            var Q5;
            Q5=makeQuery(id+"F22.boolean.opBoolean","INTERSECT",EDGE,{"derivedFrom":[makeQuery(id+"F14.opExtrude","SWEPT_FACE",FACE,{"disambiguationData":[OSD([sQuery(id+"F13.wireOp",EDGE,"E17.0.3.2")])]}),makeQuery(id+"F22.opExtrude","SWEPT_FACE",FACE,{"disambiguationData":[OSD([sQuery(id+"F21.wireOp",EDGE,"E24.bottom")])]})]});
            var Q6;
            Q6=makeQuery(id+"F22.boolean.opBoolean","INTERSECT",EDGE,{"derivedFrom":[makeQuery(id+"F11.opExtrude","SWEPT_FACE",FACE,{"disambiguationData":[OSD([sQuery(id+"F10.wireOp",EDGE,"E14.0.2.5")])]}),makeQuery(id+"F22.opExtrude","SWEPT_FACE",FACE,{"disambiguationData":[OSD([sQuery(id+"F21.wireOp",EDGE,"E24.top")])]})]});
            var Q7;
            Q7=makeQuery(id+"F22.boolean.opBoolean","INTERSECT",EDGE,{"derivedFrom":[makeQuery(id+"F14.opExtrude","SWEPT_FACE",FACE,{"disambiguationData":[OSD([sQuery(id+"F13.wireOp",EDGE,"E17.0.2.4")])]}),makeQuery(id+"F22.opExtrude","SWEPT_FACE",FACE,{"disambiguationData":[OSD([sQuery(id+"F21.wireOp",EDGE,"E24.top")])]})]});
            var Q8;
            Q8=makeQuery(id+"F14.opExtrude","SWEPT_EDGE",EDGE,{"disambiguationData":[OSD([sQuery(id+"F13.wireOp",EDGE,"E17.0.1.4"),sQuery(id+"F13.wireOp",EDGE,"E17.0.1.7")])]});
            var Q9;
            Q9=makeQuery(id+"F11.opExtrude","SWEPT_EDGE",EDGE,{"disambiguationData":[OSD([sQuery(id+"F10.wireOp",EDGE,"E14.0.1.5"),sQuery(id+"F10.wireOp",EDGE,"E14.0.1.7")])]});
            var Q10;
            Q10=makeQuery(id+"F11.opExtrude","SWEPT_EDGE",EDGE,{"disambiguationData":[OSD([sQuery(id+"F10.wireOp",EDGE,"E13.bottom"),sQuery(id+"F10.wireOp",EDGE,"E13.right")])]});
            var Q11;
            Q11=makeQuery(id+"F14.opExtrude","SWEPT_EDGE",EDGE,{"disambiguationData":[OSD([sQuery(id+"F13.wireOp",EDGE,"E16.bottom"),sQuery(id+"F13.wireOp",EDGE,"E16.right")])]});
            var Q12;
            Q12=makeQuery(id+"F6.opExtrude","SWEPT_EDGE",EDGE,{"disambiguationData":[OSD([sQuery(id+"F5.wireOp",EDGE,"E4.top"),sQuery(id+"F5.wireOp",EDGE,"E4.left")])]});
            var Q13;
            Q13=makeQuery(id+"F6.opExtrude","SWEPT_EDGE",EDGE,{"disambiguationData":[OSD([sQuery(id+"F5.wireOp",EDGE,"E3.top"),sQuery(id+"F5.wireOp",EDGE,"E3.left")])]});
            var Q14;
            Q14=makeQuery(id+"F22.boolean.opBoolean","INTERSECT",EDGE,{"derivedFrom":[makeQuery(id+"F3.boolean.opBoolean","COPY",FACE,{"derivedFrom":makeQuery(id+"F3.opExtrude","SWEPT_FACE",FACE,{"disambiguationData":[OSD([sQuery(id+"F2.wireOp",EDGE,"E1.left")])]})}),makeQuery(id+"F22.opExtrude","SWEPT_FACE",FACE,{"disambiguationData":[OSD([sQuery(id+"F21.wireOp",EDGE,"E24.top")])]})]});
            var Q15;
            {var subQ0=sQuery(id+"F2.wireOp",EDGE,"E1.right");Q15=makeQuery(id+"F4.opFillet","BLEND_EDGE",EDGE,{"blendedFrom":[makeQuery(id+"F3.boolean.opBoolean","COPY",EDGE,{"derivedFrom":makeQuery(id+"F3.opExtrude","SWEPT_EDGE",EDGE,{"disambiguationData":[OSD([sQuery(id+"F2.wireOp",EDGE,"E1.bottom"),subQ0])]})}),makeQuery(id+"F3.boolean.opBoolean","COPY",FACE,{"derivedFrom":makeQuery(id+"F3.opExtrude","SWEPT_FACE",FACE,{"disambiguationData":[OSD([subQ0])]})})],"blendedInto":[makeQuery(id+"F3.boolean.opBoolean","COPY",FACE,{"derivedFrom":makeQuery(id+"F3.opExtrude","SWEPT_FACE",FACE,{"disambiguationData":[OSD([subQ0])]})})]});}
            var Q16;
            Q16=makeQuery(id+"F22.boolean.opBoolean","INTERSECT",EDGE,{"derivedFrom":[makeQuery(id+"F3.boolean.opBoolean","COPY",FACE,{"derivedFrom":makeQuery(id+"F3.opExtrude","SWEPT_FACE",FACE,{"disambiguationData":[OSD([sQuery(id+"F2.wireOp",EDGE,"E1.right")])]})}),makeQuery(id+"F22.opExtrude","SWEPT_FACE",FACE,{"disambiguationData":[OSD([sQuery(id+"F21.wireOp",EDGE,"E24.top")])]})]});
            var Q17;
            Q17=makeQuery(id+"F6.opExtrude","SWEPT_EDGE",EDGE,{"disambiguationData":[OSD([sQuery(id+"F5.wireOp",EDGE,"E3.top"),sQuery(id+"F5.wireOp",EDGE,"E3.right")])]});
            var Q18;
            Q18=makeQuery(id+"F6.opExtrude","SWEPT_EDGE",EDGE,{"disambiguationData":[OSD([sQuery(id+"F5.wireOp",EDGE,"E4.top"),sQuery(id+"F5.wireOp",EDGE,"E4.right")])]});
            var Q19;
            Q19=makeQuery(id+"F14.boolean.opBoolean","INTERSECT",EDGE,{"derivedFrom":[makeQuery(id+"F6.opExtrude","SWEPT_FACE",FACE,{"disambiguationData":[OSD([sQuery(id+"F5.wireOp",EDGE,"E3.bottom")])]}),makeQuery(id+"F14.opExtrude","SWEPT_FACE",FACE,{"disambiguationData":[OSD([sQuery(id+"F13.wireOp",EDGE,"E17.0.2.0")])]})]});
            var Q20;
            Q20=makeQuery(id+"F11.boolean.opBoolean","INTERSECT",EDGE,{"derivedFrom":[makeQuery(id+"F6.opExtrude","SWEPT_FACE",FACE,{"disambiguationData":[OSD([sQuery(id+"F5.wireOp",EDGE,"E3.bottom")])]}),makeQuery(id+"F11.opExtrude","SWEPT_FACE",FACE,{"disambiguationData":[OSD([sQuery(id+"F10.wireOp",EDGE,"E14.0.2.0")])]})]});
            var Q21;
            Q21=makeQuery(id+"F11.boolean.opBoolean","INTERSECT",EDGE,{"derivedFrom":[makeQuery(id+"F6.opExtrude","SWEPT_FACE",FACE,{"disambiguationData":[OSD([sQuery(id+"F5.wireOp",EDGE,"E4.bottom")])]}),makeQuery(id+"F11.opExtrude","SWEPT_FACE",FACE,{"disambiguationData":[OSD([sQuery(id+"F10.wireOp",EDGE,"E14.0.1.0")])]})]});
            var Q22;
            Q22=makeQuery(id+"F14.boolean.opBoolean","INTERSECT",EDGE,{"derivedFrom":[makeQuery(id+"F6.opExtrude","SWEPT_FACE",FACE,{"disambiguationData":[OSD([sQuery(id+"F5.wireOp",EDGE,"E4.bottom")])]}),makeQuery(id+"F14.opExtrude","SWEPT_FACE",FACE,{"disambiguationData":[OSD([sQuery(id+"F13.wireOp",EDGE,"E17.0.1.0")])]})]});
            var Q23;
            Q23=makeQuery(id+"F14.opExtrude","SWEPT_EDGE",EDGE,{"disambiguationData":[OSD([sQuery(id+"F13.wireOp",EDGE,"E15.bottom"),sQuery(id+"F13.wireOp",EDGE,"E15.right")])]});
            var Q24;
            Q24=makeQuery(id+"F11.opExtrude","SWEPT_EDGE",EDGE,{"disambiguationData":[OSD([sQuery(id+"F10.wireOp",EDGE,"E12.bottom"),sQuery(id+"F10.wireOp",EDGE,"E12.right")])]});
            var Q25;
            Q25=makeQuery(id+"F6.opExtrude","SWEPT_EDGE",EDGE,{"disambiguationData":[OSD([sQuery(id+"F5.wireOp",EDGE,"E4.bottom"),sQuery(id+"F5.wireOp",EDGE,"E4.left")])]});
            var Q26;
            Q26=makeQuery(id+"F6.opExtrude","SWEPT_EDGE",EDGE,{"disambiguationData":[OSD([sQuery(id+"F5.wireOp",EDGE,"E3.bottom"),sQuery(id+"F5.wireOp",EDGE,"E3.left")])]});
            var Q27;
            Q27=makeQuery(id+"F6.opExtrude","SWEPT_EDGE",EDGE,{"disambiguationData":[OSD([sQuery(id+"F5.wireOp",EDGE,"E4.bottom"),sQuery(id+"F5.wireOp",EDGE,"E4.right")])]});
            var Q28;
            Q28=makeQuery(id+"F6.opExtrude","SWEPT_EDGE",EDGE,{"disambiguationData":[OSD([sQuery(id+"F5.wireOp",EDGE,"E3.bottom"),sQuery(id+"F5.wireOp",EDGE,"E3.right")])]});
            var Q29;
            Q29=makeQuery(id+"F22.boolean.opBoolean","INTERSECT",EDGE,{"derivedFrom":[makeQuery(id+"F3.boolean.opBoolean","COPY",FACE,{"derivedFrom":makeQuery(id+"F3.opExtrude","SWEPT_FACE",FACE,{"disambiguationData":[OSD([sQuery(id+"F2.wireOp",EDGE,"E1.right")])]})}),makeQuery(id+"F22.opExtrude","SWEPT_FACE",FACE,{"disambiguationData":[OSD([sQuery(id+"F21.wireOp",EDGE,"E24.bottom")])]})]});
            var Q30;
            {var subQ0=sQuery(id+"F2.wireOp",EDGE,"E1.left");Q30=makeQuery(id+"F4.opFillet","BLEND_EDGE",EDGE,{"blendedFrom":[makeQuery(id+"F3.boolean.opBoolean","COPY",EDGE,{"derivedFrom":makeQuery(id+"F3.opExtrude","SWEPT_EDGE",EDGE,{"disambiguationData":[OSD([sQuery(id+"F2.wireOp",EDGE,"E1.bottom"),subQ0])]})}),makeQuery(id+"F3.boolean.opBoolean","COPY",FACE,{"derivedFrom":makeQuery(id+"F3.opExtrude","SWEPT_FACE",FACE,{"disambiguationData":[OSD([subQ0])]})})],"blendedInto":[makeQuery(id+"F3.boolean.opBoolean","COPY",FACE,{"derivedFrom":makeQuery(id+"F3.opExtrude","SWEPT_FACE",FACE,{"disambiguationData":[OSD([subQ0])]})})]});}
            var Q31;
            Q31=makeQuery(id+"F22.boolean.opBoolean","INTERSECT",EDGE,{"derivedFrom":[makeQuery(id+"F3.boolean.opBoolean","COPY",FACE,{"derivedFrom":makeQuery(id+"F3.opExtrude","SWEPT_FACE",FACE,{"disambiguationData":[OSD([sQuery(id+"F2.wireOp",EDGE,"E1.left")])]})}),makeQuery(id+"F22.opExtrude","SWEPT_FACE",FACE,{"disambiguationData":[OSD([sQuery(id+"F21.wireOp",EDGE,"E24.bottom")])]})]});
            fillet(context, id + "F23", {"entities" : qUnion([Q0, Q1, Q2, Q3, Q4, Q5, Q6, Q7, Q8, Q9, Q10, Q11, Q12, Q13, Q14, Q15, Q16, Q17, Q18, Q19, Q20, Q21, Q22, Q23, Q24, Q25, Q26, Q27, Q28, Q29, Q30, Q31]), "radius" : 0.76 * mm, "tangentPropagation" : true, "allowEdgeOverflow" : false});
        }
        {
            var Q0;
            Q0=makeQuery(id+"F1.opExtrude","SWEPT_FACE",FACE,{"disambiguationData":[OSD([sQuery(id+"F0.wireOp",EDGE,"E0.left")])]});
            var sketch = newSketch(context, id + "F24", { "sketchPlane" : qUnion([Q0])});
            skCircle(sketch, "E25", {"center": v(-130.28, 30.75) * mm, "radius": 5.72 * mm});
            skSolve(sketch);
        }
        {
            var Q0;
            Q0 = qSketchRegion(id + "F24", true);
            extrude(context, id + "F25", {"entities" : qUnion([Q0]), "operationType" : NewBodyOperationType.REMOVE, "oppositeDirection" : true, "depth" : 177.8 * mm, "offsetDistance" : 25.4 * mm});
        }
        {
            var Q0;
            {var subQ0=sQuery(id+"F0.wireOp",EDGE,"E0.top");var subQ1=makeQuery(id+"F1.opExtrude","SWEPT_FACE",FACE,{"disambiguationData":[OSD([subQ0])]});var subQ3=sQuery(id+"F17.wireOp",EDGE,"E19.bottom");var subQ4=makeQuery(id+"F18.opExtrude","SWEPT_FACE",FACE,{"disambiguationData":[OSD([subQ3])]});var subQ8=sQuery(id+"F17.wireOp",EDGE,"E19.right");Q0=makeQuery(id+"F20.boolean.opBoolean","MERGE",FACE,{"derivedFrom":[makeQuery(id+"F18.boolean.opBoolean","SPLIT",FACE,{"disambiguationData":[TD([makeQuery(id+"F18.opExtrude","SWEPT_FACE",FACE,{"disambiguationData":[OSD([subQ8])]})])],"derivedFrom":subQ4}),makeQuery(id+"F18.boolean.opBoolean","SPLIT",FACE,{"disambiguationData":[TD([makeQuery(id+"FzKzKi3lcmixfaw_1.boolean.opBoolean","COPY",FACE,{"disambiguationData":[TD([subQ1])],"derivedFrom":makeQuery(id+"FzKzKi3lcmixfaw_1.opExtrude","SWEPT_FACE",FACE,{"disambiguationData":[OSD([sQuery(id+"F9.wireOp",EDGE,"E10")])]})})])],"derivedFrom":subQ4}),makeQuery(id+"F18.boolean.opBoolean","SPLIT",FACE,{"disambiguationData":[TD([makeQuery(id+"FzKzKi3lcmixfaw_1.boolean.opBoolean","COPY",FACE,{"disambiguationData":[TD([subQ1])],"derivedFrom":makeQuery(id+"FzKzKi3lcmixfaw_1.opExtrude","SWEPT_FACE",FACE,{"disambiguationData":[OSD([sQuery(id+"F9.wireOp",EDGE,"E11")])]})})])],"derivedFrom":subQ4}),makeQuery(id+"F20.opExtrude","SWEPT_FACE",FACE,{"disambiguationData":[OSD([sQuery(id+"F19.wireOp",EDGE,"E20")])]})]});}
            var sketch = newSketch(context, id + "F26", { "sketchPlane" : qUnion([Q0])});
            skCircle(sketch, "E26", {"center": v(-38.05, 5.72) * mm, "radius": 2.02 * mm});
            skSolve(sketch);
        }
        {
            var Q0;
            Q0=makeQuery(id+"F18.boolean.opBoolean","MERGE",FACE,{"derivedFrom":[makeQuery(id+"F1.opExtrude","CAP_FACE",FACE,{"disambiguationData":[OSD([sQuery(id+"F0.wireOp",EDGE,"E0.bottom"),sQuery(id+"F0.wireOp",EDGE,"E0.top"),sQuery(id+"F0.wireOp",EDGE,"E0.left"),sQuery(id+"F0.wireOp",EDGE,"E0.right")])],"isStart":true}),makeQuery(id+"F18.opExtrude","CAP_FACE",FACE,{"disambiguationData":[OSD([sQuery(id+"F17.wireOp",EDGE,"E19.bottom"),sQuery(id+"F17.wireOp",EDGE,"E19.top"),sQuery(id+"F17.wireOp",EDGE,"E19.left"),sQuery(id+"F17.wireOp",EDGE,"E19.right")])],"isStart":true})]});
            var sketch = newSketch(context, id + "F27", { "sketchPlane" : qUnion([Q0])});
            skLineSegment(sketch, "E27.bottom", {"start": v(35.56, -3.18) * mm, "end": v(40.64, -3.18) * mm});
            skLineSegment(sketch, "E27.top", {"start": v(35.56, -8.26) * mm, "end": v(40.64, -8.26) * mm});
            skLineSegment(sketch, "E27.left", {"start": v(35.56, -3.18) * mm, "end": v(35.56, -8.26) * mm});
            skLineSegment(sketch, "E27.right", {"start": v(40.64, -3.18) * mm, "end": v(40.64, -8.26) * mm});
            skLineSegment(sketch, "E28.bottom", {"start": v(35.56, -168.28) * mm, "end": v(40.64, -168.28) * mm});
            skLineSegment(sketch, "E28.top", {"start": v(35.56, -163.2) * mm, "end": v(40.64, -163.2) * mm});
            skLineSegment(sketch, "E28.left", {"start": v(35.56, -168.28) * mm, "end": v(35.56, -163.2) * mm});
            skLineSegment(sketch, "E28.right", {"start": v(40.64, -168.28) * mm, "end": v(40.64, -163.2) * mm});
            skSolve(sketch);
        }
        {
            var Q0;
            Q0 = qSketchRegion(id + "F27", true);
            extrude(context, id + "F28", {"entities" : qUnion([Q0]), "operationType" : NewBodyOperationType.ADD, "oppositeDirection" : true, "depth" : 8.9 * mm, "offsetDistance" : 25.4 * mm});
        }
        {
            var Q0;
            Q0 = qSketchRegion(id + "F16", true);
            extrude(context, id + "F29", {"entities" : qUnion([Q0]), "operationType" : NewBodyOperationType.REMOVE, "oppositeDirection" : true, "depth" : 8.9 * mm, "offsetDistance" : 25.4 * mm});
        }
        {
            var Q0;
            Q0 = qSketchRegion(id + "F26", true);
            extrude(context, id + "F30", {"entities" : qUnion([Q0]), "operationType" : NewBodyOperationType.REMOVE, "oppositeDirection" : true, "depth" : 8.9 * mm, "offsetDistance" : 25.4 * mm});
        }
        {
            var Q0;
            Q0 = qSketchRegion(id + "F9", true);
            extrude(context, id + "F31", {"entities" : qUnion([Q0]), "operationType" : NewBodyOperationType.REMOVE, "oppositeDirection" : true, "depth" : 177.8 * mm, "offsetDistance" : 25.4 * mm});
        }
        {
            var Q0;
            Q0=makeQuery(id+"F1.opExtrude","SWEPT_FACE",FACE,{"disambiguationData":[OSD([sQuery(id+"F0.wireOp",EDGE,"E0.left")])]});
            var sketch = newSketch(context, id + "F32", { "sketchPlane" : qUnion([Q0])});
            skCircle(sketch, "E29", {"center": v(-151.99, 33.38) * mm, "radius": 1.59 * mm});
            skCircle(sketch, "E30", {"center": v(-108.97, 33.38) * mm, "radius": 1.59 * mm});
            skCircle(sketch, "E31", {"center": v(-65.96, 33.38) * mm, "radius": 1.59 * mm});
            skCircle(sketch, "E32", {"center": v(-23.25, 33.38) * mm, "radius": 1.59 * mm});
            skSolve(sketch);
        }
        {
            var Q0;
            Q0 = qSketchRegion(id + "F32", true);
            extrude(context, id + "F33", {"entities" : qUnion([Q0]), "operationType" : NewBodyOperationType.REMOVE, "oppositeDirection" : true, "depth" : 5.08 * mm, "offsetDistance" : 25.4 * mm});
        }
        {
            var Q0;
            Q0=makeQuery(id+"F20.boolean.opBoolean","MERGE",FACE,{"derivedFrom":[makeQuery(id+"F18.opExtrude","SWEPT_FACE",FACE,{"disambiguationData":[OSD([sQuery(id+"F17.wireOp",EDGE,"E19.bottom")])]}),makeQuery(id+"F20.opExtrude","SWEPT_FACE",FACE,{"disambiguationData":[OSD([sQuery(id+"F19.wireOp",EDGE,"E20")])]})]});
            var sketch = newSketch(context, id + "F34", { "sketchPlane" : qUnion([Q0])});
            skCircle(sketch, "E33", {"center": v(-9.53, 28.58) * mm, "radius": 2.54 * mm});
            skCircle(sketch, "E34", {"center": v(-165.11, 28.58) * mm, "radius": 2.54 * mm});
            skSolve(sketch);
        }
        {
            var Q0;
            Q0 = qSketchRegion(id + "F34", true);
            extrude(context, id + "F35", {"entities" : qUnion([Q0]), "operationType" : NewBodyOperationType.REMOVE, "oppositeDirection" : true, "depth" : 5.08 * mm, "offsetDistance" : 25.4 * mm});
        }
    });
